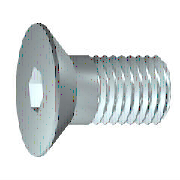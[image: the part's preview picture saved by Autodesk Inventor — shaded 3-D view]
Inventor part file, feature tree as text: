
AUTODESK INVENTOR PART (.ipt)
format: ipt  version: 2012 (Build 160160000, 160)  size: 181,248 bytes
history: native  units: mm (DEFAULTED — no unit token found)
features: extrude x1, plane x1
ambient origin geometry x7: Origin, YZ Plane, XY Plane, X Axis, Y Axis, Z Axis, Center Point
bodies: Solid1 (feature_tree), Body (feature_tree)
feature tree (2):
  extrude  "Slot"  Depth=15.875mm
  plane  "Work Plane1"
